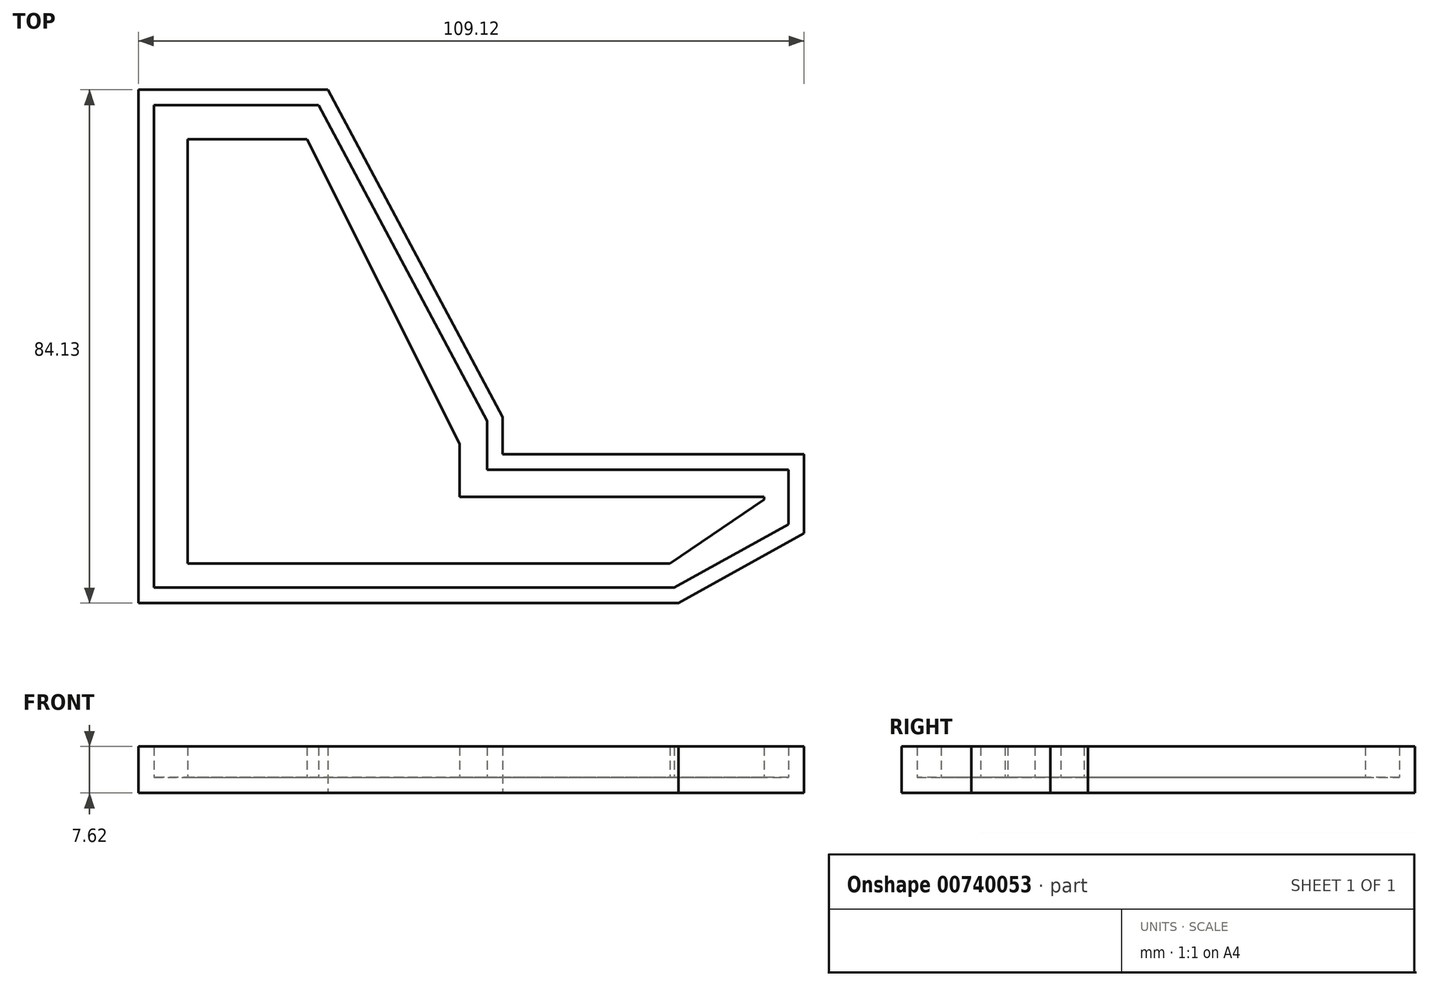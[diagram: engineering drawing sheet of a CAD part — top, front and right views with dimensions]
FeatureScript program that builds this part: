
annotation { "Feature Type Name" : "Feature", "Feature Type Description" : "" }
export const myFeature = defineFeature(function(context is Context, id is Id, definition is map)
    precondition{}
    {
        {
            var Q0;
            Q0=qCreatedBy(makeId("Top.planeOp"),FACE);
            var sketch = newSketch(context, id + "F0", { "sketchPlane" : qUnion([Q0])});
            skLineSegment(sketch, "E0", {"start": v(3.44, 39.29) * mm, "end": v(-27.66, 39.29) * mm});
            skLineSegment(sketch, "E1", {"start": v(-27.66, 39.29) * mm, "end": v(-27.66, -44.84) * mm});
            skLineSegment(sketch, "E2", {"start": v(-27.66, -44.84) * mm, "end": v(60.85, -44.84) * mm});
            skLineSegment(sketch, "E3", {"start": v(60.85, -44.84) * mm, "end": v(81.46, -33.4) * mm});
            skLineSegment(sketch, "E4", {"start": v(81.46, -33.4) * mm, "end": v(81.46, -20.44) * mm});
            skLineSegment(sketch, "E5", {"start": v(81.46, -20.44) * mm, "end": v(32.07, -20.44) * mm});
            skLineSegment(sketch, "E6", {"start": v(32.07, -20.44) * mm, "end": v(32.07, -14.32) * mm});
            skLineSegment(sketch, "E7", {"start": v(32.07, -14.32) * mm, "end": v(3.44, 39.29) * mm});
            skSolve(sketch);
        }
        {
            var Q0;
            Q0 = qSketchRegion(id + "F0", true);
            extrude(context, id + "F1", {"entities" : qUnion([Q0]), "depth" : 7.62 * mm, "offsetDistance" : 25.4 * mm});
        }
        {
            var Q0;
            Q0=makeQuery(id+"F1.opExtrude","CAP_FACE",FACE,{"disambiguationData":[OSD([sQuery(id+"F0.wireOp",EDGE,"E0"),sQuery(id+"F0.wireOp",EDGE,"E1"),sQuery(id+"F0.wireOp",EDGE,"E2"),sQuery(id+"F0.wireOp",EDGE,"E3"),sQuery(id+"F0.wireOp",EDGE,"E4"),sQuery(id+"F0.wireOp",EDGE,"E5"),sQuery(id+"F0.wireOp",EDGE,"E6"),sQuery(id+"F0.wireOp",EDGE,"E7")])],"isStart":false});
            shell(context, id + "F2", {"entities" : qUnion([Q0]), "thickness" : 2.54 * mm});
        }
        {
            var Q0;
            Q0=makeQuery(id+"F2.opShell","OFFSET_FACE",FACE,{"disambiguationData":[OSD([sQuery(id+"F0.wireOp",EDGE,"E0"),sQuery(id+"F0.wireOp",EDGE,"E1"),sQuery(id+"F0.wireOp",EDGE,"E2"),sQuery(id+"F0.wireOp",EDGE,"E3"),sQuery(id+"F0.wireOp",EDGE,"E4"),sQuery(id+"F0.wireOp",EDGE,"E5"),sQuery(id+"F0.wireOp",EDGE,"E6"),sQuery(id+"F0.wireOp",EDGE,"E7")])]});
            var sketch = newSketch(context, id + "F3", { "sketchPlane" : qUnion([Q0])});
            skLineSegment(sketch, "E8", {"start": v(0, 31.18) * mm, "end": v(-19.56, 31.18) * mm});
            skLineSegment(sketch, "E9", {"start": v(-19.56, 31.18) * mm, "end": v(-19.56, -38.36) * mm});
            skLineSegment(sketch, "E10", {"start": v(-19.56, -38.36) * mm, "end": v(59.49, -38.36) * mm});
            skLineSegment(sketch, "E11", {"start": v(59.49, -38.36) * mm, "end": v(74.94, -27.9) * mm});
            skLineSegment(sketch, "E12", {"start": v(74.94, -27.9) * mm, "end": v(74.94, -27.45) * mm});
            skLineSegment(sketch, "E13", {"start": v(74.94, -27.45) * mm, "end": v(25.04, -27.45) * mm});
            skLineSegment(sketch, "E14", {"start": v(25.04, -27.45) * mm, "end": v(25.04, -18.72) * mm});
            skLineSegment(sketch, "E15", {"start": v(25.04, -18.72) * mm, "end": v(0, 31.18) * mm});
            skPoint(sketch, "E16", {"position": v(78.92, -27.45) * mm});
            skSolve(sketch);
        }
        {
            var Q0;
            Q0=makeQuery(id+"F3.imprint","IMPRINT",FACE,{"disambiguationData":[TD([[makeQuery(id+"F3.imprint","IMPRINT",EDGE,{"derivedFrom":sQuery(id+"F3.wireOp",EDGE,"E8")}),1.0]])]});
            extrude(context, id + "F4", {"entities" : qUnion([Q0]), "operationType" : NewBodyOperationType.ADD, "depth" : 5.08 * mm, "offsetDistance" : 25.4 * mm});
        }
    });
